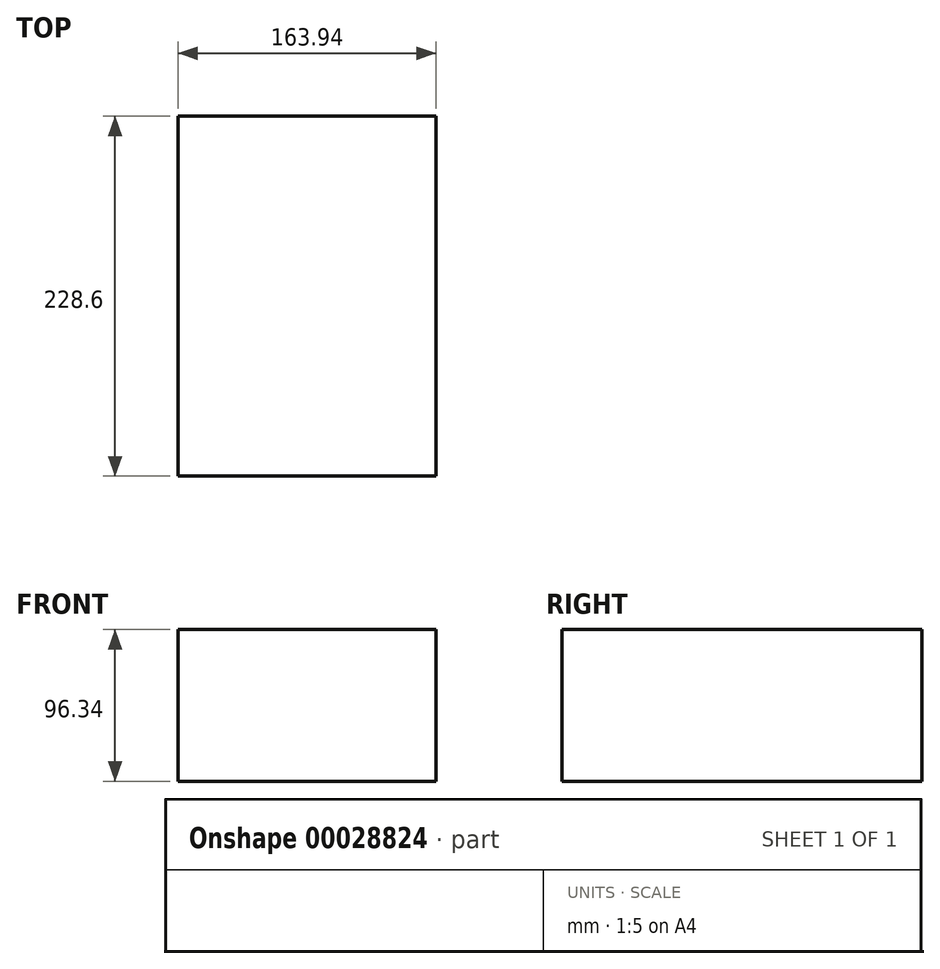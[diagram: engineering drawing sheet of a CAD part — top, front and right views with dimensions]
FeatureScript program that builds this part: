
annotation { "Feature Type Name" : "Feature", "Feature Type Description" : "" }
export const myFeature = defineFeature(function(context is Context, id is Id, definition is map)
    precondition{}
    {
        {
            var Q0;
            Q0=qCreatedBy(makeId("Front.planeOp"),FACE);
            var sketch = newSketch(context, id + "F0", { "sketchPlane" : qUnion([Q0])});
            skLineSegment(sketch, "E0.bottom", {"start": v(-85.44, 50.31) * mm, "end": v(78.5, 50.31) * mm});
            skLineSegment(sketch, "E0.top", {"start": v(-85.44, -46.03) * mm, "end": v(78.5, -46.03) * mm});
            skLineSegment(sketch, "E0.left", {"start": v(-85.44, 50.31) * mm, "end": v(-85.44, -46.03) * mm});
            skLineSegment(sketch, "E0.right", {"start": v(78.5, 50.31) * mm, "end": v(78.5, -46.03) * mm});
            skSolve(sketch);
        }
        {
            var Q0;
            Q0=makeQuery(id+"F0.imprint","IMPRINT",FACE,{"disambiguationData":[TD([[makeQuery(id+"F0.imprint","IMPRINT",EDGE,{"derivedFrom":sQuery(id+"F0.wireOp",EDGE,"E0.bottom")}),-1.0]])]});
            var Q1;
            Q1=makeQuery(id+"F0.imprint","IMPRINT",FACE,{"disambiguationData":[TD([[makeQuery(id+"F0.imprint","IMPRINT",EDGE,{"derivedFrom":sQuery(id+"F0.wireOp",EDGE,"8a69531f-fdea-49b4-bf2a-b80b7cd3eaa6")}),1.0]])]});
            extrude(context, id + "F1", {"entities" : qUnion([Q0, Q1]), "depth" : 228.6 * mm});
        }
    });
